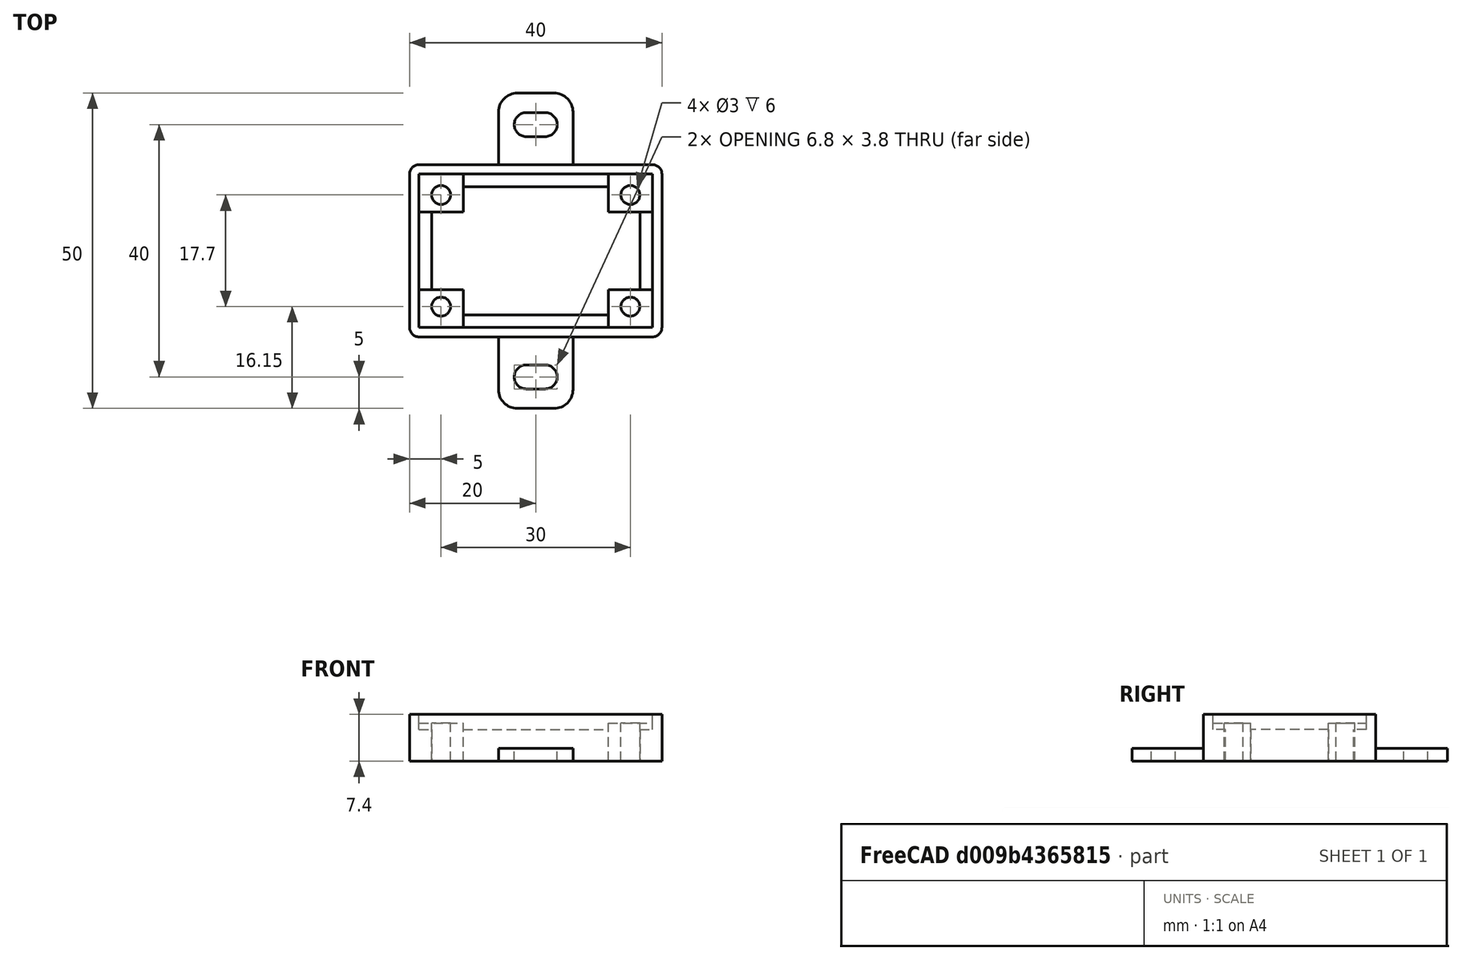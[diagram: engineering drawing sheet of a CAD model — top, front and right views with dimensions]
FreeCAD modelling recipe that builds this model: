
FCSTD DOCUMENT  (FreeCAD 0.19R23578 (Git))
Label: neo-6m-0-001
License: All rights reserved
LicenseURL: http://en.wikipedia.org/wiki/All_rights_reserved
objects: Part::Box×4, Part::MultiFuse×3, Part::FeaturePython×2, Part::Cut×2, Spreadsheet::Sheet×1, Part::Cylinder×1, Part::Fillet×1, Part::Feature×1, App::Part×1
note: 14 computed .brp shape members not serialized (recipe doc carries the construction recipe); baked Part::Feature solids carry a one-line shape summary decoded from their .brp

FEATURE [Spreadsheet::Sheet] Spreadsheet  label="p"
  cells = A1=hole_x_dist; B1(hole_x_dist)=30; A2=hole_y_dist; B2(hole_y_dist)=17.7; A3=pcb_under; B3(pcb_under)=3; A4=pcb_x; B4(pcb_x)=37; A5=pcb_y; B5(pcb_y)=24.3; A6=hole_stand_x; B6(hole_stand_x)=7; A7=hole_stand_y; B7(hole_stand_y)=6; A8=hole_r; B8(hole_r)=1.5; A9=box_wall; B9(box_wall)=1.5; A10=under_layer; B10(under_layer)=3; A11=pcb_height; B11(pcb_height)=1.4; A12=under_pcb_border; B12(under_pcb_border)=2
FEATURE [Part::Box] Box  label="bottom cube"
  AttacherType = Attacher::AttachEngine3D
  Height = 7.4
  Length = 40
  Width = 27.3
  expr: Width = <<p>>.pcb_y + <<p>>.box_wall * 2
  expr: Length = <<p>>.pcb_x + <<p>>.box_wall * 2
  expr: Height = <<p>>.pcb_under + <<p>>.pcb_height + <<p>>.under_layer
FEATURE [Part::Box] Box001  label="bottom extraction"
  AttacherType = Attacher::AttachEngine3D
  Height = 10
  Length = 33
  Placement = pos=(3.5,3.5,0) rot=(0,0,1;0rad)
  Width = 20.3
  expr: .Placement.Base.y = <<p>>.under_pcb_border + <<p>>.box_wall
  expr: .Placement.Base.x = <<p>>.under_pcb_border + <<p>>.box_wall
  expr: Length = <<p>>.pcb_x - <<p>>.under_pcb_border * 2
  expr: Width = <<p>>.pcb_y - <<p>>.under_pcb_border * 2
FEATURE [Part::Box] Box002  label="pcb extraction"
  AttacherType = Attacher::AttachEngine3D
  Height = 10
  Length = 37
  Placement = pos=(1.5,1.5,5) rot=(0,0,1;0rad)
  Width = 24.3
  expr: .Placement.Base.z = <<p>>.under_pcb_border + <<p>>.under_layer
  expr: .Placement.Base.y = <<p>>.box_wall
  expr: .Placement.Base.x = <<p>>.box_wall
  expr: Length = <<p>>.pcb_x
  expr: Width = <<p>>.pcb_y
FEATURE [Part::MultiFuse] Fusion  label="bottom extraction001"
  Shapes = -> [Box001,Box002]
FEATURE [Part::Box] Box003  label="hole stand cube"
  AttacherType = Attacher::AttachEngine3D
  Height = 6
  Length = 7
  Placement = pos=(1.5,1.5,0) rot=(0,0,1;0rad)
  Width = 6
  expr: .Placement.Base.y = <<p>>.box_wall
  expr: .Placement.Base.x = <<p>>.box_wall
  expr: Height = <<p>>.pcb_under + <<p>>.under_layer
  expr: Width = <<p>>.hole_stand_y
  expr: Length = <<p>>.hole_stand_x
FEATURE [Part::FeaturePython] Array  label="hole stand array"  # Draft array (typed FeaturePython)
  Angle = 360
  ArrayType = 0
  Axis = (0,0,1)
  Base = -> Box003
  Center = (0,0,0)
  Fuse = false
  IntervalAxis = (0,0,0)
  IntervalX = (30,0,0)
  IntervalY = (0,18.3,0)
  IntervalZ = (0,0,1)
  NumberPolar = 1
  NumberX = 2
  NumberY = 2
  NumberZ = 1
  expr: .IntervalY.y = <<p>>.pcb_y - <<p>>.hole_stand_y
  expr: .IntervalX.x = <<p>>.pcb_x - <<p>>.hole_stand_x
FEATURE [Part::Cylinder] Cylinder  label="pcb hole"
  Angle = 360
  AttacherType = Attacher::AttachEngine3D
  Height = 10
  Placement = pos=(5,4.8,0) rot=(0,0,1;0rad)
  Radius = 1.5
  expr: .Placement.Base.y = (<<p>>.box_wall * 2 + <<p>>.pcb_y - <<p>>.hole_y_dist) / 2
  expr: .Placement.Base.x = (<<p>>.box_wall * 2 + <<p>>.pcb_x - <<p>>.hole_x_dist) / 2
  expr: Radius = <<p>>.hole_r
FEATURE [Part::FeaturePython] Array001  label="hole array"  # Draft array (typed FeaturePython)
  Angle = 360
  ArrayType = 0
  Axis = (0,0,1)
  Base = -> Cylinder
  Center = (0,0,0)
  Fuse = false
  IntervalAxis = (0,0,0)
  IntervalX = (30,0,0)
  IntervalY = (0,17.7,0)
  IntervalZ = (0,0,1)
  NumberPolar = 1
  NumberX = 2
  NumberY = 2
  NumberZ = 1
  expr: .IntervalY.y = <<p>>.hole_y_dist
  expr: .IntervalX.x = <<p>>.hole_x_dist
FEATURE [Part::Fillet] Fillet001  label="bottom cube fillet"
  Base = -> Box
  Edges = 4 edges r=1.5: [Edge1,Edge3,Edge5,Edge7]
FEATURE [Part::Feature] Cut002001  label="attach plane y dir001"
  Placement = pos=(14.1,-11.35,0) rot=(0,0,1;0rad)
  shape: bbox 11.8 x 50 x 2 mm, 20 faces (baked)
FEATURE [Part::MultiFuse] Fusion002  label="bottom fusion"
  Shapes = -> [Fillet001,Cut002001]
FEATURE [Part::Cut] Cut  label="pcb box cut"
  Base = -> Fusion002
  Tool = -> Fusion
FEATURE [Part::MultiFuse] Fusion001  label="frame fusion"
  Shapes = -> [Array,Cut]
FEATURE [Part::Cut] Cut001  label="frame fusion with holes"
  Base = -> Fusion001
  Tool = -> Array001
FEATURE [App::Part] Part  label="neo-6m-0-001 with 4 holes part"
  Group = -> [Fusion,Fusion002,Box002,Box003,Box001,Array001,Box,Cut,Array,Cylinder,Fusion001,Cut001]
  Origin = -> Origin
